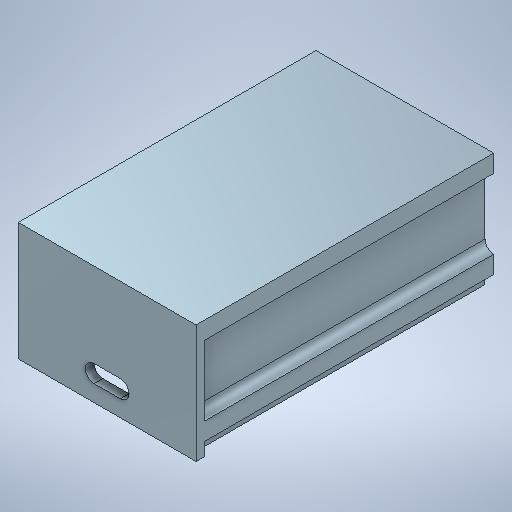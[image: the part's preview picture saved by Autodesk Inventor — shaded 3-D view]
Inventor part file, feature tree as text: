
AUTODESK INVENTOR PART (.ipt)
format: ipt  version: 2025.1 (Build 291241020, 241B)  size: 328,192 bytes
history: native  units: mm
features: extrude x5, sketch x5, mirror x2, fillet x1, plane x1, projected_geometry x1
ambient origin geometry x8: Origin, YZ Plane, XZ Plane, XY Plane, X Axis, Y Axis, Z Axis, Center Point
bodies: Solid1 (feature_tree)
feature tree (15):
  extrude  "Extrusion1"  Depth=2.0mm
  mirror  "Mirror1"
  extrude  "Extrusion2"  Depth=3.0mm
  fillet  "Fillet1"  Radius=3.0mm
  plane  "Work Plane1"
  mirror  "Mirror2"
  extrude  "Extrusion3"  Depth=66.0mm TaperAngle=0.0deg
  extrude  "Extrusion4"  Depth=2.0mm
  extrude  "Extrusion5"  Depth=4.0mm
  sketch  "Sketch1"  dims[d1=27.0mm d4=2.0mm]
  sketch  "Sketch2"  dims[d9=17.5mm d10=2.2mm d11=3.0mm]
  sketch  "Sketch3"  dims[d12=3.2mm d13=66.0mm d14=0.0mm]
  projected_geometry  "Projected Loop1"
  sketch  "Sketch4"  dims[d15=4.0mm d16=2.0mm]
  sketch  "Sketch5"  dims[d17=2.0mm d18=4.0mm d19=2.0mm d20=66.0mm d21=0.0mm d22=2.0mm d23=20.0mm d24=5.0mm d26=15.0mm d27=5.0mm d28=15.0mm d29=0.0mm d30=2.0mm d31=15.0mm d32=0.0mm d33=4.0mm d34=10.0mm d35=7.75mm d36=10.0mm d37=0.0mm]
